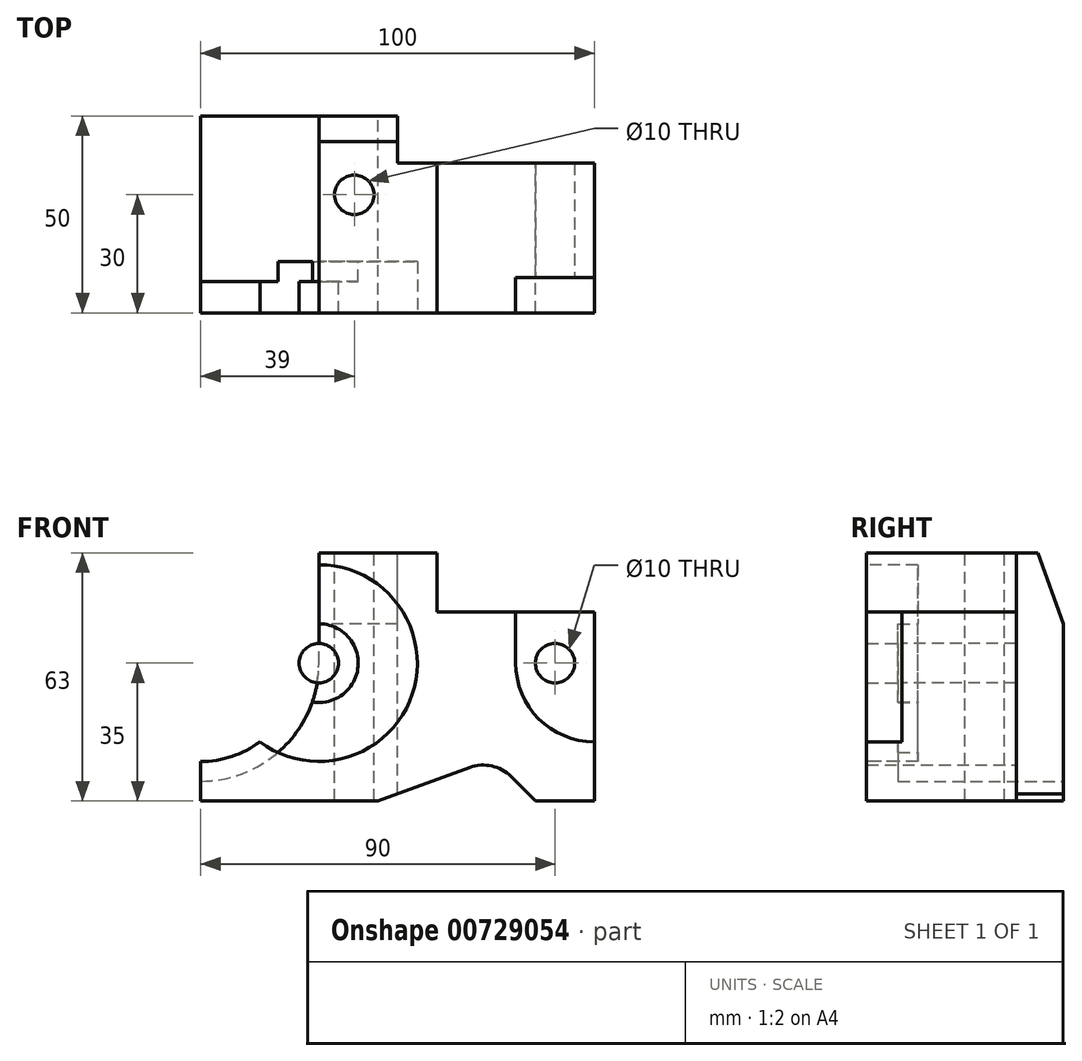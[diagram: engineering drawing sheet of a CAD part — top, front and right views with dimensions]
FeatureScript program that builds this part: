
annotation { "Feature Type Name" : "Feature", "Feature Type Description" : "" }
export const myFeature = defineFeature(function(context is Context, id is Id, definition is map)
    precondition{}
    {
        {
            assignVariable(context, id + "F0", {"name" : "B", "anyValue" : 50});
        }
        {
            var Q0;
            Q0=qCreatedBy(makeId("Front.planeOp"),FACE);
            var sketch = newSketch(context, id + "F1", { "sketchPlane" : qUnion([Q0])});
            skLineSegment(sketch, "E0", {"start": v(0, 0) * mm, "end": v(-15, 0) * mm});
            skLineSegment(sketch, "E1", {"start": v(-15, 0) * mm, "end": v(-21.17, 6.17) * mm});
            skArc(sketch, "E2", {"start": v(-21.17, 6.17) * mm, "mid": v(-26.08, 8.86) * mm, "end": v(-31.66, 8.5) * mm});
            skLineSegment(sketch, "E3", {"start": v(-31.66, 8.5) * mm, "end": v(-55, 0) * mm});
            skLineSegment(sketch, "E4", {"start": v(-55, 0) * mm, "end": v(-100, 0) * mm});
            skLineSegment(sketch, "E5", {"start": v(-100, 0) * mm, "end": v(-100, 63) * mm});
            skLineSegment(sketch, "E6", {"start": v(-100, 63) * mm, "end": v(-40, 63) * mm});
            skLineSegment(sketch, "E7", {"start": v(-40, 63) * mm, "end": v(-40, 48) * mm});
            skLineSegment(sketch, "E8", {"start": v(-40, 48) * mm, "end": v(0, 48) * mm});
            skLineSegment(sketch, "E9", {"start": v(0, 48) * mm, "end": v(0, 0) * mm});
            skSolve(sketch);
        }
        {
            var Q0;
            Q0 = qSketchRegion(id + "F1", true);
            extrude(context, id + "F2", {"entities" : qUnion([Q0]), "depth" : 50 * mm, "offsetDistance" : 25 * mm});
        }
        {
            var Q0;
            Q0=makeQuery(id+"F2.opExtrude","CAP_FACE",FACE,{"disambiguationData":[OSD([sQuery(id+"F1.wireOp",EDGE,"E0"),sQuery(id+"F1.wireOp",EDGE,"E1"),sQuery(id+"F1.wireOp",EDGE,"E2"),sQuery(id+"F1.wireOp",EDGE,"E3"),sQuery(id+"F1.wireOp",EDGE,"E4"),sQuery(id+"F1.wireOp",EDGE,"E5"),sQuery(id+"F1.wireOp",EDGE,"E6"),sQuery(id+"F1.wireOp",EDGE,"E7"),sQuery(id+"F1.wireOp",EDGE,"E8"),sQuery(id+"F1.wireOp",EDGE,"E9")])],"isStart":false});
            var sketch = newSketch(context, id + "F3", { "sketchPlane" : qUnion([Q0])});
            skLineSegment(sketch, "E10", {"start": v(0, 0) * mm, "end": v(0, 15) * mm});
            skLineSegment(sketch, "E11", {"start": v(-20, 48) * mm, "end": v(-20, 35) * mm});
            skArc(sketch, "E12", {"start": v(-20, 35) * mm, "mid": v(-14.14, 20.86) * mm, "end": v(0, 15) * mm});
            skLineSegment(sketch, "E13", {"start": v(-20, 48) * mm, "end": v(0, 48) * mm});
            skLineSegment(sketch, "E14", {"start": v(0, 48) * mm, "end": v(0, 15) * mm});
            skSolve(sketch);
        }
        {
            var Q0;
            Q0 = qSketchRegion(id + "F3", true);
            extrude(context, id + "F4", {"entities" : qUnion([Q0]), "operationType" : NewBodyOperationType.REMOVE, "oppositeDirection" : true, "depth" : 9 * mm, "offsetDistance" : 25 * mm});
        }
        {
            var Q0;
            Q0=makeQuery(id+"F4.boolean.opBoolean","COPY",FACE,{"derivedFrom":makeQuery(id+"F4.opExtrude","CAP_FACE",FACE,{"disambiguationData":[OSD([sQuery(id+"F3.wireOp",EDGE,"E11"),sQuery(id+"F3.wireOp",EDGE,"E12"),sQuery(id+"F3.wireOp",EDGE,"E13"),sQuery(id+"F3.wireOp",EDGE,"E14")])],"isStart":false})});
            var sketch = newSketch(context, id + "F5", { "sketchPlane" : qUnion([Q0])});
            skCircle(sketch, "E15", {"center": v(-10, 35) * mm, "radius": 5 * mm});
            skSolve(sketch);
        }
        {
            var Q0;
            Q0 = qSketchRegion(id + "F5", true);
            extrude(context, id + "F6", {"entities" : qUnion([Q0]), "operationType" : NewBodyOperationType.REMOVE, "endBound" : BoundingType.THROUGH_ALL, "oppositeDirection" : true, "depth" : 25 * mm, "offsetDistance" : 25 * mm});
        }
        {
            var Q0;
            Q0=makeQuery(id+"F2.opExtrude","CAP_FACE",FACE,{"disambiguationData":[OSD([sQuery(id+"F1.wireOp",EDGE,"E0"),sQuery(id+"F1.wireOp",EDGE,"E1"),sQuery(id+"F1.wireOp",EDGE,"E2"),sQuery(id+"F1.wireOp",EDGE,"E3"),sQuery(id+"F1.wireOp",EDGE,"E4"),sQuery(id+"F1.wireOp",EDGE,"E5"),sQuery(id+"F1.wireOp",EDGE,"E6"),sQuery(id+"F1.wireOp",EDGE,"E7"),sQuery(id+"F1.wireOp",EDGE,"E8"),sQuery(id+"F1.wireOp",EDGE,"E9")])],"isStart":false});
            var sketch = newSketch(context, id + "F7", { "sketchPlane" : qUnion([Q0])});
            skCircle(sketch, "E16", {"center": v(-70, 35) * mm, "radius": 25 * mm});
            skSolve(sketch);
        }
        {
            var Q0;
            Q0 = qSketchRegion(id + "F7", true);
            extrude(context, id + "F8", {"entities" : qUnion([Q0]), "operationType" : NewBodyOperationType.REMOVE, "oppositeDirection" : true, "depth" : 13 * mm, "offsetDistance" : 25 * mm});
        }
        {
            var Q0;
            Q0=makeQuery(id+"F8.boolean.opBoolean","COPY",FACE,{"derivedFrom":makeQuery(id+"F8.opExtrude","CAP_FACE",FACE,{"disambiguationData":[OSD([sQuery(id+"F7.wireOp",EDGE,"E16")])],"isStart":false})});
            var sketch = newSketch(context, id + "F9", { "sketchPlane" : qUnion([Q0])});
            skCircle(sketch, "E17", {"center": v(-70, 35) * mm, "radius": 10 * mm});
            skSolve(sketch);
        }
        {
            var Q0;
            Q0 = qSketchRegion(id + "F9", true);
            extrude(context, id + "F10", {"entities" : qUnion([Q0]), "operationType" : NewBodyOperationType.ADD, "depth" : 5 * mm, "offsetDistance" : 25 * mm});
        }
        {
            var Q0;
            Q0=makeQuery(id+"F10.opExtrude","CAP_FACE",FACE,{"disambiguationData":[OSD([sQuery(id+"F9.wireOp",EDGE,"E17")])],"isStart":false});
            var sketch = newSketch(context, id + "F11", { "sketchPlane" : qUnion([Q0])});
            skCircle(sketch, "E18", {"center": v(-70, 35) * mm, "radius": 5 * mm});
            skSolve(sketch);
        }
        {
            var Q0;
            Q0 = qSketchRegion(id + "F11", true);
            extrude(context, id + "F12", {"entities" : qUnion([Q0]), "operationType" : NewBodyOperationType.ADD, "depth" : 8 * mm, "offsetDistance" : 25 * mm});
        }
        {
            var Q0;
            Q0=makeQuery(id+"F2.opExtrude","CAP_FACE",FACE,{"disambiguationData":[OSD([sQuery(id+"F1.wireOp",EDGE,"E0"),sQuery(id+"F1.wireOp",EDGE,"E1"),sQuery(id+"F1.wireOp",EDGE,"E2"),sQuery(id+"F1.wireOp",EDGE,"E3"),sQuery(id+"F1.wireOp",EDGE,"E4"),sQuery(id+"F1.wireOp",EDGE,"E5"),sQuery(id+"F1.wireOp",EDGE,"E6"),sQuery(id+"F1.wireOp",EDGE,"E7"),sQuery(id+"F1.wireOp",EDGE,"E8"),sQuery(id+"F1.wireOp",EDGE,"E9")])],"isStart":false});
            var sketch = newSketch(context, id + "F13", { "sketchPlane" : qUnion([Q0])});
            skCircle(sketch, "E19", {"center": v(-100, 35) * mm, "radius": 25 * mm});
            skSolve(sketch);
        }
        {
            var Q0;
            Q0 = qSketchRegion(id + "F13", true);
            extrude(context, id + "F14", {"entities" : qUnion([Q0]), "operationType" : NewBodyOperationType.REMOVE, "endBound" : BoundingType.THROUGH_ALL, "oppositeDirection" : true, "depth" : 25 * mm, "offsetDistance" : 25 * mm});
        }
        {
            var Q0;
            Q0=makeQuery(id+"F2.opExtrude","CAP_FACE",FACE,{"disambiguationData":[OSD([sQuery(id+"F1.wireOp",EDGE,"E0"),sQuery(id+"F1.wireOp",EDGE,"E1"),sQuery(id+"F1.wireOp",EDGE,"E2"),sQuery(id+"F1.wireOp",EDGE,"E3"),sQuery(id+"F1.wireOp",EDGE,"E4"),sQuery(id+"F1.wireOp",EDGE,"E5"),sQuery(id+"F1.wireOp",EDGE,"E6"),sQuery(id+"F1.wireOp",EDGE,"E7"),sQuery(id+"F1.wireOp",EDGE,"E8"),sQuery(id+"F1.wireOp",EDGE,"E9")])],"isStart":true});
            var sketch = newSketch(context, id + "F15", { "sketchPlane" : qUnion([Q0])});
            skArc(sketch, "E20", {"start": v(70, 35) * mm, "mid": v(121.21, 13.79) * mm, "end": v(100, 65) * mm});
            skLineSegment(sketch, "E21", {"start": v(70, 35) * mm, "end": v(70, 73.91) * mm});
            skLineSegment(sketch, "E22", {"start": v(70, 73.91) * mm, "end": v(100, 73.91) * mm});
            skLineSegment(sketch, "E23", {"start": v(100, 73.91) * mm, "end": v(100, 65) * mm});
            skSolve(sketch);
        }
        {
            var Q0;
            Q0 = qSketchRegion(id + "F15", true);
            extrude(context, id + "F16", {"entities" : qUnion([Q0]), "operationType" : NewBodyOperationType.REMOVE, "oppositeDirection" : true, "depth" : (getVariable(context, 'B') - 8) * mm, "offsetDistance" : 25 * mm});
        }
        {
            var Q0;
            {var subQ0=sQuery(id+"F15.wireOp",EDGE,"E21");Q0=makeQuery(id+"F16.boolean.opBoolean","COPY",FACE,{"disambiguationData":[TD([makeQuery(id+"F2.opExtrude","SWEPT_FACE",FACE,{"disambiguationData":[OSD([sQuery(id+"F1.wireOp",EDGE,"E5")])]}),makeQuery(id+"F2.opExtrude","SWEPT_FACE",FACE,{"disambiguationData":[OSD([sQuery(id+"F1.wireOp",EDGE,"E6")])]}),makeQuery(id+"F8.boolean.opBoolean","COPY",FACE,{"derivedFrom":makeQuery(id+"F8.opExtrude","SWEPT_FACE",FACE,{"disambiguationData":[OSD([sQuery(id+"F7.wireOp",EDGE,"E16")])]})}),makeQuery(id+"F14.boolean.opBoolean","COPY",FACE,{"derivedFrom":makeQuery(id+"F14.opExtrude","SWEPT_FACE",FACE,{"disambiguationData":[OSD([sQuery(id+"F13.wireOp",EDGE,"E19")])]})}),makeQuery(id+"F16.opExtrude","SWEPT_FACE",FACE,{"disambiguationData":[OSD([subQ0])]})])],"derivedFrom":makeQuery(id+"F16.opExtrude","CAP_FACE",FACE,{"disambiguationData":[OSD([sQuery(id+"F15.wireOp",EDGE,"E20"),subQ0,sQuery(id+"F15.wireOp",EDGE,"E22"),sQuery(id+"F15.wireOp",EDGE,"E23")])],"isStart":false})});}
            var sketch = newSketch(context, id + "F17", { "sketchPlane" : qUnion([Q0])});
            skLineSegment(sketch, "E24.0.0", {"start": v(70, 63) * mm, "end": v(70, 60) * mm});
            skArc(sketch, "E24.0.1", {"start": v(70, 60) * mm, "mid": v(77.9, 58.72) * mm, "end": v(85, 55) * mm});
            skArc(sketch, "E24.0.2", {"start": v(85, 55) * mm, "mid": v(92.1, 58.72) * mm, "end": v(100, 60) * mm});
            skLineSegment(sketch, "E24.0.3", {"start": v(100, 60) * mm, "end": v(100, 63) * mm});
            skLineSegment(sketch, "E24.0.4", {"start": v(100, 63) * mm, "end": v(70, 63) * mm});
            skSolve(sketch);
        }
        {
            var Q0;
            Q0 = qSketchRegion(id + "F17", true);
            var Q1;
            Q1=makeQuery(id+"F2.opExtrude","CAP_FACE",FACE,{"disambiguationData":[OSD([sQuery(id+"F1.wireOp",EDGE,"E0"),sQuery(id+"F1.wireOp",EDGE,"E1"),sQuery(id+"F1.wireOp",EDGE,"E2"),sQuery(id+"F1.wireOp",EDGE,"E3"),sQuery(id+"F1.wireOp",EDGE,"E4"),sQuery(id+"F1.wireOp",EDGE,"E5"),sQuery(id+"F1.wireOp",EDGE,"E6"),sQuery(id+"F1.wireOp",EDGE,"E7"),sQuery(id+"F1.wireOp",EDGE,"E8"),sQuery(id+"F1.wireOp",EDGE,"E9")])],"isStart":false});
            extrude(context, id + "F18", {"entities" : qUnion([Q0]), "operationType" : NewBodyOperationType.REMOVE, "endBound" : BoundingType.UP_TO_SURFACE, "oppositeDirection" : true, "depth" : 25 * mm, "endBoundEntityFace" : qUnion([Q1]), "offsetDistance" : 25 * mm});
        }
        {
            var Q0;
            Q0=makeQuery(id+"F2.opExtrude","SWEPT_FACE",FACE,{"disambiguationData":[OSD([sQuery(id+"F1.wireOp",EDGE,"E6")])]});
            var sketch = newSketch(context, id + "F19", { "sketchPlane" : qUnion([Q0])});
            skCircle(sketch, "E25", {"center": v(-61, -20) * mm, "radius": 5 * mm});
            skSolve(sketch);
        }
        {
            var Q0;
            Q0 = qSketchRegion(id + "F19", true);
            extrude(context, id + "F20", {"entities" : qUnion([Q0]), "operationType" : NewBodyOperationType.REMOVE, "endBound" : BoundingType.THROUGH_ALL, "oppositeDirection" : true, "depth" : 25 * mm, "offsetDistance" : 25 * mm});
        }
        {
            var Q0;
            Q0=makeQuery(id+"F2.opExtrude","SWEPT_FACE",FACE,{"disambiguationData":[OSD([sQuery(id+"F1.wireOp",EDGE,"E6")])]});
            var sketch = newSketch(context, id + "F21", { "sketchPlane" : qUnion([Q0])});
            skLineSegment(sketch, "E26.bottom", {"start": v(0, 0) * mm, "end": v(-50, 0) * mm});
            skLineSegment(sketch, "E26.top", {"start": v(0, -12) * mm, "end": v(-50, -12) * mm});
            skLineSegment(sketch, "E26.left", {"start": v(0, 0) * mm, "end": v(0, -12) * mm});
            skLineSegment(sketch, "E26.right", {"start": v(-50, 0) * mm, "end": v(-50, -12) * mm});
            skSolve(sketch);
        }
        {
            var Q0;
            Q0 = qSketchRegion(id + "F21", true);
            extrude(context, id + "F22", {"entities" : qUnion([Q0]), "operationType" : NewBodyOperationType.REMOVE, "endBound" : BoundingType.THROUGH_ALL, "oppositeDirection" : true, "depth" : 25 * mm, "offsetDistance" : 25 * mm});
        }
        {
            var Q0;
            Q0=makeQuery(id+"F18.boolean.opBoolean","MERGE",FACE,{"derivedFrom":[makeQuery(id+"F16.boolean.opBoolean","COPY",FACE,{"derivedFrom":makeQuery(id+"F16.opExtrude","SWEPT_FACE",FACE,{"disambiguationData":[OSD([sQuery(id+"F15.wireOp",EDGE,"E21")])]})}),makeQuery(id+"F18.opExtrude","SWEPT_FACE",FACE,{"disambiguationData":[OSD([sQuery(id+"F17.wireOp",EDGE,"E24.0.0")])]})]});
            var sketch = newSketch(context, id + "F23", { "sketchPlane" : qUnion([Q0])});
            skLineSegment(sketch, "E27", {"start": v(0, 63) * mm, "end": v(0, 45) * mm});
            skLineSegment(sketch, "E28", {"start": v(0, 45) * mm, "end": v(6.55, 63) * mm});
            skLineSegment(sketch, "E29", {"start": v(6.55, 63) * mm, "end": v(0, 63) * mm});
            skSolve(sketch);
        }
        {
            var Q0;
            Q0 = qSketchRegion(id + "F23", true);
            extrude(context, id + "F24", {"entities" : qUnion([Q0]), "operationType" : NewBodyOperationType.REMOVE, "endBound" : BoundingType.THROUGH_ALL, "oppositeDirection" : true, "depth" : 25 * mm, "offsetDistance" : 25 * mm});
        }
    });
